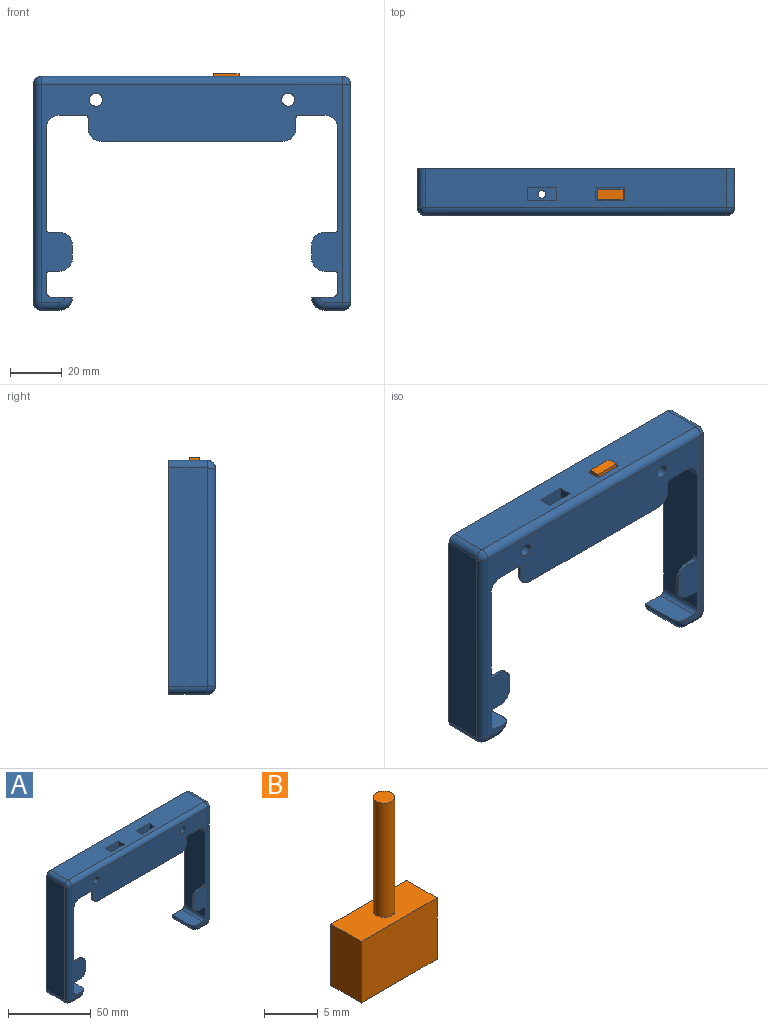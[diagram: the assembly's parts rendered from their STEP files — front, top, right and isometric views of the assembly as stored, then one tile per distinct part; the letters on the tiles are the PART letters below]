
ASSEMBLY  parts=2 mates=1
PART A: 78 faces, bbox 122x18x90 mm
  f0: plane 102x18mm, normal (0,0,-1), area 1641.5mm2, adj f6,f9,f18,f24,f47,f48,f49,f76
  f1: plane 116.2x15mm, normal (0,0,1), area 1633mm2, adj f9,f15,f34,f35,f66,f67,f68,f69
  f2: cylinder r=3mm len=7.2mm, axis (-1,0,0), area 33.2mm2, adj f3,f4,f5,f6
  f3: plane 15x7.2mm, normal (0,0,-1), area 108mm2, adj f2,f7,f8,f9
  f4: bspline ~3.27x3.27mm, area 13.9mm2, adj f2,f7,f10
  f5: revolved ~4.9x4.9mm, area 28.2mm2, adj f2,f6,f8,f11
  f6: plane 116x84mm, normal (0,-1,0), area 2748.7mm2, adj f0,f2,f5,f10,f11,f12,f13,f14
  f7: cylinder r=2.9mm len=15mm, axis (0,-1,0), area 68.3mm2, adj f3,f4,f9,f27
  f8: cylinder r=4.9mm len=15mm, axis (0,-1,0), area 115.5mm2, adj f3,f5,f9,f28
  f9: plane 122x90mm, normal (0,1,0), area 2635.7mm2, adj f0,f1,f3,f7,f8,f12,f13,f14
  f10: cylinder r=3mm len=84.2mm, axis (0,0,1), area 395.2mm2, adj f4,f6,f27,f36
  f11: cylinder r=3mm len=3mm, axis (0,0,-1), area 0.5mm2, adj f5,f6,f12,f28
  f12: plane 18x8mm, normal (0,0,1), area 142.1mm2, adj f6,f9,f11,f13,f28
  f13: cylinder r=2mm len=18mm, axis (0,-1,0), area 56.5mm2, adj f6,f9,f12,f14
  f14: plane 63x18mm, normal (1,0,0), area 1096.6mm2, adj f6,f9,f13,f18,f37,f38,f39
  f15: cylinder r=3mm len=116.2mm, axis (1,0,0), area 546mm2, adj f1,f6,f36,f45
  f16: cylinder r=3mm len=84.2mm, axis (0,0,-1), area 395.2mm2, adj f6,f32,f45,f46
  f17: cylinder r=3mm len=7.2mm, axis (-1,0,0), area 33.2mm2, adj f6,f19,f29,f46
  f18: cylinder r=5mm len=18mm, axis (0,-1,0), area 141.4mm2, adj f0,f6,f9,f14
  f19: revolved ~4.9x4.9mm, area 28.2mm2, adj f6,f17,f20,f31
  f20: cylinder r=3mm len=3mm, axis (0,0,1), area 0.5mm2, adj f6,f19,f21,f33
  f21: plane 18x8mm, normal (0,0,1), area 142.1mm2, adj f6,f9,f20,f22,f33
  f22: cylinder r=2mm len=18mm, axis (0,-1,0), area 56.5mm2, adj f6,f9,f21,f23
  f23: plane 63x18mm, normal (-1,0,0), area 1096.6mm2, adj f6,f9,f22,f24,f55,f56,f57
  f24: cylinder r=5mm len=18mm, axis (0,-1,0), area 141.4mm2, adj f0,f6,f9,f23
  f25: cylinder r=2.5mm len=18mm, axis (0,1,0), area 282.7mm2, adj f6,f9
  f26: cylinder r=2.5mm len=18mm, axis (0,1,0), area 282.7mm2, adj f6,f9
  f27: plane 84.2x15mm, normal (-1,0,0), area 1263mm2, adj f7,f9,f10,f35
  f28: plane 15x0.1mm, normal (1,0,0), area 1.5mm2, adj f8,f9,f11,f12
  f29: plane 15x7.2mm, normal (0,0,-1), area 108mm2, adj f9,f17,f30,f31
  f30: cylinder r=2.9mm len=15mm, axis (0,-1,0), area 68.3mm2, adj f9,f29,f32,f46
  f31: cylinder r=4.9mm len=15mm, axis (0,-1,0), area 115.5mm2, adj f9,f19,f29,f33
  f32: plane 84.2x15mm, normal (1,0,0), area 1263mm2, adj f9,f16,f30,f34
  f33: plane 15x0.1mm, normal (-1,0,0), area 1.5mm2, adj f9,f20,f21,f31
  f34: cylinder r=2.9mm len=15mm, axis (0,-1,0), area 68.3mm2, adj f1,f9,f32,f45
  f35: cylinder r=2.9mm len=15mm, axis (0,-1,0), area 68.3mm2, adj f1,f9,f27,f36
  f36: bspline ~3.27x3.27mm, area 13.9mm2, adj f10,f15,f35
  f37: cylinder r=1mm len=2.2mm, axis (0,-1,0), area 2.7mm2, adj f6,f14,f39,f40
  f38: cylinder r=1mm len=2.2mm, axis (0,1,0), area 2.7mm2, adj f6,f14,f39,f44
  f39: cylinder r=1mm len=17mm, axis (0,0,-1), area 25.1mm2, adj f14,f37,f38,f63
  f40: plane 4x1.2mm, normal (0,0,-1), area 4.8mm2, adj f6,f37,f41,f63
  f41: cylinder r=5mm len=5mm, axis (0,-1,0), area 9.4mm2, adj f6,f40,f42,f63
  f42: plane 5x1.2mm, normal (1,0,0), area 6mm2, adj f6,f41,f43,f63
  f43: cylinder r=5mm len=5mm, axis (0,1,0), area 9.4mm2, adj f6,f42,f44,f63
  f44: plane 4x1.2mm, normal (0,0,1), area 4.8mm2, adj f6,f38,f43,f63
  f45: bspline ~3.27x3.27mm, area 14.6mm2, adj f15,f16,f34
  f46: bspline ~3.27x3.27mm, area 13.9mm2, adj f16,f17,f30
  f47: cylinder r=1mm len=2.2mm, axis (0,1,0), area 2.7mm2, adj f0,f6,f48,f54
  f48: cylinder r=1mm len=82mm, axis (-1,0,0), area 127.2mm2, adj f0,f47,f49,f64
  f49: cylinder r=1mm len=2.2mm, axis (0,-1,0), area 2.7mm2, adj f0,f6,f48,f50
  f50: plane 4x1.2mm, normal (-1,0,0), area 4.8mm2, adj f6,f49,f51,f64
  f51: cylinder r=5mm len=5mm, axis (0,-1,0), area 9.4mm2, adj f6,f50,f52,f64
  f52: plane 70x1.2mm, normal (0,0,-1), area 84mm2, adj f6,f51,f53,f64
  f53: cylinder r=5mm len=5mm, axis (0,1,0), area 9.4mm2, adj f6,f52,f54,f64
  f54: plane 4x1.2mm, normal (1,0,0), area 4.8mm2, adj f6,f47,f53,f64
  f55: cylinder r=1mm len=2.2mm, axis (0,-1,0), area 2.7mm2, adj f6,f23,f57,f58
  f56: cylinder r=1mm len=2.2mm, axis (0,1,0), area 2.7mm2, adj f6,f23,f57,f62
  f57: cylinder r=1mm len=17mm, axis (0,0,-1), area 25.1mm2, adj f23,f55,f56,f65
  f58: plane 4x1.2mm, normal (0,0,-1), area 4.8mm2, adj f6,f55,f59,f65
  f59: cylinder r=5mm len=5mm, axis (0,-1,0), area 9.4mm2, adj f6,f58,f60,f65
  f60: plane 5x1.2mm, normal (-1,0,0), area 6mm2, adj f6,f59,f61,f65
  f61: cylinder r=5mm len=5mm, axis (0,1,0), area 9.4mm2, adj f6,f60,f62,f65
  f62: plane 4x1.2mm, normal (0,0,1), area 4.8mm2, adj f6,f56,f61,f65
  f63: plane 15x9mm, normal (0,1,0), area 124.3mm2, adj f39,f40,f41,f42,f43,f44
  f64: plane 80x9mm, normal (0,1,0), area 709.3mm2, adj f48,f50,f51,f52,f53,f54
  f65: plane 15x9mm, normal (0,1,0), area 124.3mm2, adj f57,f58,f59,f60,f61,f62
  f66: plane 6x5mm, normal (1,0,0), area 30mm2, adj f1,f67,f69,f70
  f67: plane 11x6mm, normal (0,1,0), area 66mm2, adj f1,f66,f68,f70
  f68: plane 6x5mm, normal (-1,0,0), area 30mm2, adj f1,f67,f69,f70
  f69: plane 11x6mm, normal (0,-1,0), area 66mm2, adj f1,f66,f68,f70
  f70: plane 11x5mm, normal (0,0,1), area 47.9mm2, adj f66,f67,f68,f69,f77
  f71: plane 6x5mm, normal (-1,0,0), area 30mm2, adj f1,f72,f74,f75
  f72: plane 11x6mm, normal (0,-1,0), area 66mm2, adj f1,f71,f73,f75
  f73: plane 6x5mm, normal (1,0,0), area 30mm2, adj f1,f72,f74,f75
  f74: plane 11x6mm, normal (0,1,0), area 66mm2, adj f1,f71,f73,f75
  f75: plane 11x5mm, normal (0,0,1), area 47.9mm2, adj f71,f72,f73,f74,f76
  f76: cylinder r=1.5mm len=9mm, axis (0,0,1), area 84.8mm2, adj f0,f75
  f77: cylinder r=1.5mm len=9mm, axis (0,0,1), area 84.8mm2, adj f0,f70
PART B: 8 faces, bbox 10x4x20 mm
  f0: plane 10x7mm, normal (0,-1,0), area 70mm2, adj f1,f3,f4,f5
  f1: plane 7x4mm, normal (1,0,0), area 28mm2, adj f0,f2,f4,f5
  f2: plane 10x7mm, normal (0,1,0), area 70mm2, adj f1,f3,f4,f5
  f3: plane 7x4mm, normal (-1,0,0), area 28mm2, adj f0,f2,f4,f5
  f4: plane 10x4mm, normal (0,0,1), area 36.9mm2, adj f0,f1,f2,f3,f6
  f5: plane 10x4mm, normal (0,0,-1), area 40mm2, adj f0,f1,f2,f3
  f6: cylinder r=1mm len=13mm, axis (0,0,-1), area 81.7mm2, adj f4,f7
  f7: plane 2x2mm, normal (0,0,1), area 3.1mm2, adj f6
PLACE A at identity
PLACE B rot(axis=(-1,0,0),180deg) t=(13.1,-10,51)mm
MATE slider B.f6 <-> A.f77  axis (0,0,-1) through (13.1,-10,44)mm
